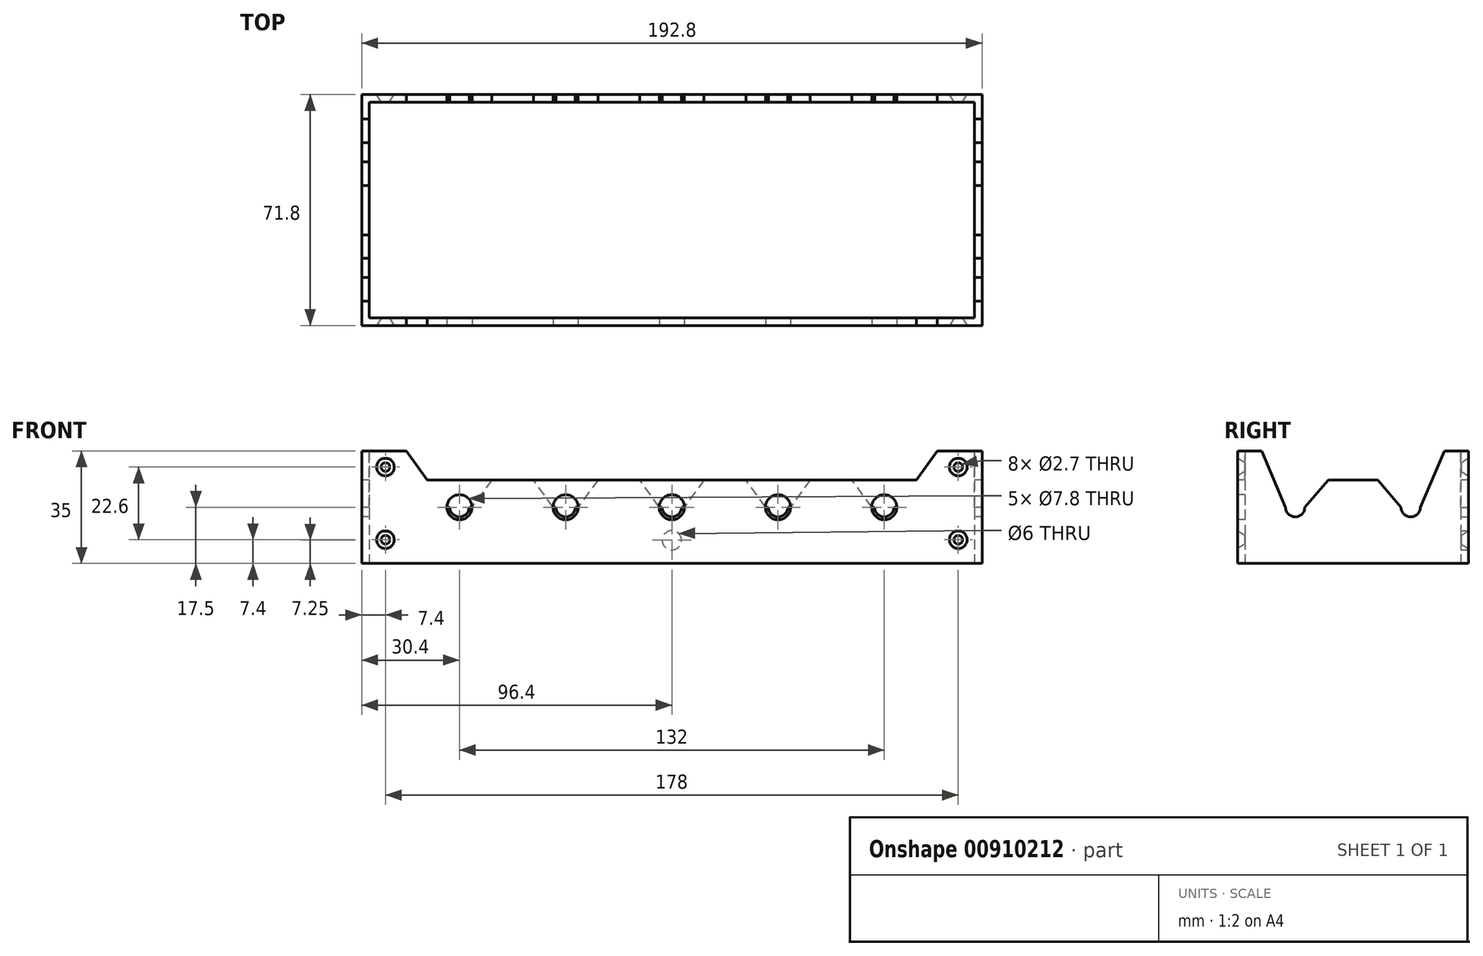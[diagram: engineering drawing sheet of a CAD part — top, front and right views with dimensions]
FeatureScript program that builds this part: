
annotation { "Feature Type Name" : "Feature", "Feature Type Description" : "" }
export const myFeature = defineFeature(function(context is Context, id is Id, definition is map)
    precondition{}
    {
        {
            var Q0;
            Q0=qCreatedBy(makeId("Top.planeOp"),FACE);
            var sketch = newSketch(context, id + "F0", { "sketchPlane" : qUnion([Q0])});
            skLineSegment(sketch, "E0.bottom", {"start": v(-94, 33.5) * mm, "end": v(94, 33.5) * mm});
            skLineSegment(sketch, "E0.top", {"start": v(-94, -33.5) * mm, "end": v(94, -33.5) * mm});
            skLineSegment(sketch, "E0.left", {"start": v(-94, 33.5) * mm, "end": v(-94, -33.5) * mm});
            skLineSegment(sketch, "E0.right", {"start": v(94, 33.5) * mm, "end": v(94, -33.5) * mm});
            skPoint(sketch, "E0.middle", {"position": v(0, 0) * mm});
            skLineSegment(sketch, "E1.bottom", {"start": v(-96.4, 35.9) * mm, "end": v(96.4, 35.9) * mm});
            skLineSegment(sketch, "E1.top", {"start": v(-96.4, -35.9) * mm, "end": v(96.4, -35.9) * mm});
            skLineSegment(sketch, "E1.left", {"start": v(-96.4, 35.9) * mm, "end": v(-96.4, -35.9) * mm});
            skLineSegment(sketch, "E1.right", {"start": v(96.4, 35.9) * mm, "end": v(96.4, -35.9) * mm});
            skSolve(sketch);
        }
        {
            var Q0;
            Q0=makeQuery(id+"F0.imprint","IMPRINT",FACE,{"disambiguationData":[TD([[makeQuery(id+"F0.imprint","IMPRINT",EDGE,{"derivedFrom":sQuery(id+"F0.wireOp",EDGE,"E0.bottom")}),1.0]])]});
            extrude(context, id + "F1", {"entities" : qUnion([Q0]), "depth" : 35 * mm, "offsetDistance" : 25 * mm});
        }
        {
            var Q0;
            Q0=makeQuery(id+"F1.opExtrude","SWEPT_FACE",FACE,{"disambiguationData":[OSD([sQuery(id+"F0.wireOp",EDGE,"E1.left")])]});
            var sketch = newSketch(context, id + "F2", { "sketchPlane" : qUnion([Q0])});
            skLineSegment(sketch, "E2", {"start": v(-35.9, 17.5) * mm, "end": v(35.9, 17.5) * mm, "construction": true});
            skPoint(sketch, "E3", {"position": v(0, 17.5) * mm});
            skLineSegment(sketch, "E4", {"start": v(-35.9, 17.5) * mm, "end": v(0, 17.5) * mm, "construction": true});
            skLineSegment(sketch, "E5", {"start": v(0, 17.5) * mm, "end": v(35.9, 17.5) * mm, "construction": true});
            skPoint(sketch, "E6", {"position": v(-17.95, 17.5) * mm});
            skPoint(sketch, "E7", {"position": v(17.95, 17.5) * mm});
            skCircle(sketch, "E8", {"center": v(-17.95, 17.5) * mm, "radius": 3 * mm});
            skCircle(sketch, "E9", {"center": v(17.95, 17.5) * mm, "radius": 3 * mm});
            skSolve(sketch);
        }
        {
            var Q0;
            Q0=makeQuery(id+"F2.imprint","IMPRINT",FACE,{"disambiguationData":[TD([[makeQuery(id+"F2.imprint","IMPRINT",EDGE,{"derivedFrom":sQuery(id+"F2.wireOp",EDGE,"E8")}),1.0]])]});
            var Q1;
            Q1=makeQuery(id+"F2.imprint","IMPRINT",FACE,{"disambiguationData":[TD([[makeQuery(id+"F2.imprint","IMPRINT",EDGE,{"derivedFrom":sQuery(id+"F2.wireOp",EDGE,"E9")}),1.0]])]});
            extrude(context, id + "F3", {"entities" : qUnion([Q0, Q1]), "operationType" : NewBodyOperationType.REMOVE, "endBound" : BoundingType.THROUGH_ALL, "oppositeDirection" : true, "depth" : 25 * mm, "offsetDistance" : 25 * mm});
        }
        {
            var Q0;
            Q0=makeQuery(id+"F1.opExtrude","SWEPT_FACE",FACE,{"disambiguationData":[OSD([sQuery(id+"F0.wireOp",EDGE,"E1.top")])]});
            var sketch = newSketch(context, id + "F4", { "sketchPlane" : qUnion([Q0])});
            skLineSegment(sketch, "E10", {"start": v(0, 35) * mm, "end": v(0, 0) * mm, "construction": true});
            skPoint(sketch, "E11", {"position": v(0, 17.5) * mm});
            skCircle(sketch, "E12", {"center": v(0, 17.5) * mm, "radius": 3.9 * mm});
            skCircle(sketch, "E13.1.0.0", {"center": v(33, 17.5) * mm, "radius": 3.9 * mm});
            skCircle(sketch, "E13.2.0.0", {"center": v(66, 17.5) * mm, "radius": 3.9 * mm});
            skLineSegment(sketch, "E13.direction1", {"start": v(0, 17.5) * mm, "end": v(33, 17.5) * mm, "construction": true});
            skCircle(sketch, "E14.1.0.0", {"center": v(-33, 17.5) * mm, "radius": 3.9 * mm});
            skCircle(sketch, "E14.2.0.0", {"center": v(-66, 17.5) * mm, "radius": 3.9 * mm});
            skLineSegment(sketch, "E14.direction1", {"start": v(0, 17.5) * mm, "end": v(-33, 17.5) * mm, "construction": true});
            skSolve(sketch);
        }
        {
            var Q0;
            Q0=qSketchRegion(id+"F4",true);
            extrude(context, id + "F5", {"entities" : qUnion([Q0]), "operationType" : NewBodyOperationType.REMOVE, "oppositeDirection" : true, "depth" : 25 * mm, "offsetDistance" : 25 * mm});
        }
        {
            var Q0;
            Q0=makeQuery(id+"F1.opExtrude","SWEPT_FACE",FACE,{"disambiguationData":[OSD([sQuery(id+"F0.wireOp",EDGE,"E1.bottom")])]});
            var sketch = newSketch(context, id + "F6", { "sketchPlane" : qUnion([Q0])});
            skLineSegment(sketch, "E15", {"start": v(0, 35) * mm, "end": v(0, 0) * mm, "construction": true});
            skLineSegment(sketch, "E16", {"start": v(-96.4, 17.5) * mm, "end": v(96.4, 17.5) * mm, "construction": true});
            skPoint(sketch, "E17", {"position": v(0, 17.5) * mm});
            skCircle(sketch, "E18", {"center": v(0, 17.5) * mm, "radius": 3 * mm});
            skCircle(sketch, "E19.1.0.0", {"center": v(33, 17.5) * mm, "radius": 3 * mm});
            skCircle(sketch, "E19.2.0.0", {"center": v(66, 17.5) * mm, "radius": 3 * mm});
            skLineSegment(sketch, "E19.direction1", {"start": v(0, 17.5) * mm, "end": v(33, 17.5) * mm, "construction": true});
            skCircle(sketch, "E20.1.0.0", {"center": v(-33, 17.5) * mm, "radius": 3 * mm});
            skCircle(sketch, "E20.2.0.0", {"center": v(-66, 17.5) * mm, "radius": 3 * mm});
            skLineSegment(sketch, "E20.direction1", {"start": v(0, 17.5) * mm, "end": v(-33, 17.5) * mm, "construction": true});
            skSolve(sketch);
        }
        {
            var Q0;
            Q0=qSketchRegion(id+"F6",true);
            extrude(context, id + "F7", {"entities" : qUnion([Q0]), "operationType" : NewBodyOperationType.REMOVE, "oppositeDirection" : true, "depth" : 25 * mm, "offsetDistance" : 25 * mm});
        }
        {
            var Q0;
            Q0=makeQuery(id+"F1.opExtrude","CAP_FACE",FACE,{"disambiguationData":[OSD([sQuery(id+"F0.wireOp",EDGE,"E0.bottom"),sQuery(id+"F0.wireOp",EDGE,"E0.top"),sQuery(id+"F0.wireOp",EDGE,"E0.left"),sQuery(id+"F0.wireOp",EDGE,"E0.right"),sQuery(id+"F0.wireOp",EDGE,"E1.bottom"),sQuery(id+"F0.wireOp",EDGE,"E1.top"),sQuery(id+"F0.wireOp",EDGE,"E1.left"),sQuery(id+"F0.wireOp",EDGE,"E1.right")])],"isStart":false});
            var sketch = newSketch(context, id + "F8", { "sketchPlane" : qUnion([Q0])});
            skLineSegment(sketch, "E21", {"start": v(96.4, 0) * mm, "end": v(-96.4, 0) * mm, "construction": true});
            skLineSegment(sketch, "E22", {"start": v(0, -33.5) * mm, "end": v(0, 33.5) * mm, "construction": true});
            skLineSegment(sketch, "E23", {"start": v(96.4, -35.9) * mm, "end": v(96.4, 0) * mm, "construction": true});
            skLineSegment(sketch, "E24", {"start": v(96.4, 35.9) * mm, "end": v(96.4, 0) * mm, "construction": true});
            skLineSegment(sketch, "E25", {"start": v(-96.4, -35.9) * mm, "end": v(-96.4, 0) * mm, "construction": true});
            skLineSegment(sketch, "E26", {"start": v(-96.4, 35.9) * mm, "end": v(-96.4, 0) * mm, "construction": true});
            skPoint(sketch, "E27", {"position": v(96.4, -17.95) * mm});
            skPoint(sketch, "E28", {"position": v(96.4, 17.95) * mm});
            skPoint(sketch, "E29", {"position": v(-96.4, -17.95) * mm});
            skPoint(sketch, "E30", {"position": v(-96.4, 17.95) * mm});
            skCircle(sketch, "E31", {"center": v(-96.4, 35.9) * mm, "radius": 7.5 * mm, "construction": true});
            skCircle(sketch, "E32", {"center": v(-96.4, -35.9) * mm, "radius": 7.5 * mm, "construction": true});
            skCircle(sketch, "E33", {"center": v(96.4, 35.9) * mm, "radius": 7.5 * mm, "construction": true});
            skCircle(sketch, "E34", {"center": v(96.4, -35.9) * mm, "radius": 7.5 * mm, "construction": true});
            skPoint(sketch, "E35", {"position": v(-96.4, 28.4) * mm});
            skPoint(sketch, "E36", {"position": v(-96.4, -28.4) * mm});
            skPoint(sketch, "E37", {"position": v(96.4, 28.4) * mm});
            skPoint(sketch, "E38", {"position": v(96.4, -28.4) * mm});
            skPoint(sketch, "E39", {"position": v(0, 35.9) * mm});
            skPoint(sketch, "E40", {"position": v(0, -35.9) * mm});
            skPoint(sketch, "E41.1.0.0", {"position": v(33, 35.9) * mm});
            skPoint(sketch, "E41.2.0.0", {"position": v(66, 35.9) * mm});
            skLineSegment(sketch, "E41.direction1", {"start": v(0, 35.9) * mm, "end": v(33, 35.9) * mm, "construction": true});
            skPoint(sketch, "E42.1.0.0", {"position": v(-33, 35.9) * mm});
            skPoint(sketch, "E42.2.0.0", {"position": v(-66, 35.9) * mm});
            skLineSegment(sketch, "E42.direction1", {"start": v(0, 35.9) * mm, "end": v(-33, 35.9) * mm, "construction": true});
            skPoint(sketch, "E43.1.0.0", {"position": v(33, -35.9) * mm});
            skPoint(sketch, "E43.2.0.0", {"position": v(66, -35.9) * mm});
            skLineSegment(sketch, "E43.direction1", {"start": v(0, -35.9) * mm, "end": v(33, -35.9) * mm, "construction": true});
            skPoint(sketch, "E44.1.0.0", {"position": v(-33, -35.9) * mm});
            skPoint(sketch, "E44.2.0.0", {"position": v(-66, -35.9) * mm});
            skLineSegment(sketch, "E44.direction1", {"start": v(0, -35.9) * mm, "end": v(-33, -35.9) * mm, "construction": true});
            skSolve(sketch);
        }
        {
            var Q0;
            Q0=makeQuery(id+"F1.opExtrude","SWEPT_FACE",FACE,{"disambiguationData":[OSD([sQuery(id+"F0.wireOp",EDGE,"E1.left")])]});
            var sketch = newSketch(context, id + "F9", { "sketchPlane" : qUnion([Q0])});
            skPoint(sketch, "E45", {"position": v(-20.95, 17.5) * mm});
            skPoint(sketch, "E45.positionSnap0", {"position": v(-35.9, 17.5) * mm});
            skPoint(sketch, "E46", {"position": v(20.95, 17.5) * mm});
            skPoint(sketch, "E46.positionSnap0", {"position": v(35.9, 17.5) * mm});
            skPoint(sketch, "E47", {"position": v(14.95, 17.5) * mm});
            skPoint(sketch, "E48", {"position": v(-14.95, 17.5) * mm});
            skLineSegment(sketch, "E49", {"start": v(-28.37, 35) * mm, "end": v(-20.95, 17.5) * mm});
            skLineSegment(sketch, "E50", {"start": v(-14.95, 17.5) * mm, "end": v(0, 35) * mm});
            skLineSegment(sketch, "E51", {"start": v(0, 35) * mm, "end": v(14.95, 17.5) * mm});
            skLineSegment(sketch, "E52", {"start": v(20.95, 17.5) * mm, "end": v(28.32, 35) * mm});
            skLineSegment(sketch, "E53", {"start": v(-35.9, 26) * mm, "end": v(35.9, 26) * mm});
            skSolve(sketch);
        }
        {
            var Q0;
            Q0=makeQuery(id+"F1.opExtrude","SWEPT_FACE",FACE,{"disambiguationData":[OSD([sQuery(id+"F0.wireOp",EDGE,"E1.top")])]});
            var sketch = newSketch(context, id + "F10", { "sketchPlane" : qUnion([Q0])});
            skPoint(sketch, "E54", {"position": v(-69.9, 17.5) * mm});
            skPoint(sketch, "E54.positionSnap0", {"position": v(-96.4, 17.5) * mm});
            skPoint(sketch, "E55", {"position": v(-62.1, 17.5) * mm});
            skPoint(sketch, "E56", {"position": v(-36.9, 17.5) * mm});
            skPoint(sketch, "E57", {"position": v(-29.1, 17.5) * mm});
            skPoint(sketch, "E58", {"position": v(-3.9, 17.5) * mm});
            skPoint(sketch, "E59", {"position": v(3.9, 17.5) * mm});
            skPoint(sketch, "E60", {"position": v(29.1, 17.5) * mm});
            skPoint(sketch, "E61", {"position": v(36.9, 17.5) * mm});
            skPoint(sketch, "E62", {"position": v(62.1, 17.5) * mm});
            skPoint(sketch, "E63", {"position": v(69.9, 17.5) * mm});
            skPoint(sketch, "E64", {"position": v(0, 35) * mm});
            skPoint(sketch, "E65.1.0.0", {"position": v(16.5, 35) * mm});
            skPoint(sketch, "E65.2.0.0", {"position": v(33, 35) * mm});
            skPoint(sketch, "E65.3.0.0", {"position": v(49.5, 35) * mm});
            skPoint(sketch, "E65.4.0.0", {"position": v(66, 35) * mm});
            skPoint(sketch, "E65.5.0.0", {"position": v(82.5, 35) * mm});
            skLineSegment(sketch, "E65.direction1", {"start": v(0, 35) * mm, "end": v(16.5, 35) * mm, "construction": true});
            skPoint(sketch, "E66.1.0.0", {"position": v(-16.5, 35) * mm});
            skPoint(sketch, "E66.2.0.0", {"position": v(-33, 35) * mm});
            skPoint(sketch, "E66.3.0.0", {"position": v(-49.5, 35) * mm});
            skPoint(sketch, "E66.4.0.0", {"position": v(-66, 35) * mm});
            skPoint(sketch, "E66.5.0.0", {"position": v(-82.5, 35) * mm});
            skLineSegment(sketch, "E66.direction1", {"start": v(0, 35) * mm, "end": v(-16.5, 35) * mm, "construction": true});
            skLineSegment(sketch, "E67", {"start": v(-82.5, 35) * mm, "end": v(-69.9, 17.5) * mm});
            skLineSegment(sketch, "E68", {"start": v(-69.9, 17.5) * mm, "end": v(-62.1, 17.5) * mm});
            skLineSegment(sketch, "E69", {"start": v(-62.1, 17.5) * mm, "end": v(-49.5, 35) * mm});
            skLineSegment(sketch, "E70", {"start": v(-49.5, 35) * mm, "end": v(-36.9, 17.5) * mm});
            skLineSegment(sketch, "E71", {"start": v(-36.9, 17.5) * mm, "end": v(-29.1, 17.5) * mm});
            skLineSegment(sketch, "E72", {"start": v(-29.1, 17.5) * mm, "end": v(-16.5, 35) * mm});
            skLineSegment(sketch, "E73", {"start": v(-16.5, 35) * mm, "end": v(-3.9, 17.5) * mm});
            skLineSegment(sketch, "E74", {"start": v(-3.9, 17.5) * mm, "end": v(3.9, 17.5) * mm});
            skLineSegment(sketch, "E75", {"start": v(3.9, 17.5) * mm, "end": v(16.5, 35) * mm});
            skLineSegment(sketch, "E76", {"start": v(16.5, 35) * mm, "end": v(29.1, 17.5) * mm});
            skLineSegment(sketch, "E77", {"start": v(29.1, 17.5) * mm, "end": v(36.9, 17.5) * mm});
            skLineSegment(sketch, "E78", {"start": v(36.9, 17.5) * mm, "end": v(49.5, 35) * mm});
            skLineSegment(sketch, "E79", {"start": v(49.5, 35) * mm, "end": v(62.1, 17.5) * mm});
            skLineSegment(sketch, "E80", {"start": v(62.1, 17.5) * mm, "end": v(69.9, 17.5) * mm});
            skLineSegment(sketch, "E81", {"start": v(69.9, 17.5) * mm, "end": v(82.5, 35) * mm});
            skLineSegment(sketch, "E82", {"start": v(-96.4, 26) * mm, "end": v(96.4, 26) * mm});
            skLineSegment(sketch, "E83.bottom", {"start": v(-94, 2.4) * mm, "end": v(-84, 2.4) * mm});
            skLineSegment(sketch, "E83.top", {"start": v(-94, 12.4) * mm, "end": v(-84, 12.4) * mm});
            skLineSegment(sketch, "E83.left", {"start": v(-94, 2.4) * mm, "end": v(-94, 12.4) * mm});
            skLineSegment(sketch, "E83.right", {"start": v(-84, 2.4) * mm, "end": v(-84, 12.4) * mm});
            skLineSegment(sketch, "E84.bottom", {"start": v(84, 12.4) * mm, "end": v(94, 12.4) * mm});
            skLineSegment(sketch, "E84.top", {"start": v(84, 2.4) * mm, "end": v(94, 2.4) * mm});
            skLineSegment(sketch, "E84.left", {"start": v(84, 12.4) * mm, "end": v(84, 2.4) * mm});
            skLineSegment(sketch, "E84.right", {"start": v(94, 12.4) * mm, "end": v(94, 2.4) * mm});
            skLineSegment(sketch, "E85.bottom", {"start": v(-94, 35) * mm, "end": v(-84, 35) * mm});
            skLineSegment(sketch, "E85.top", {"start": v(-94, 25) * mm, "end": v(-84, 25) * mm});
            skLineSegment(sketch, "E85.left", {"start": v(-94, 35) * mm, "end": v(-94, 25) * mm});
            skLineSegment(sketch, "E85.right", {"start": v(-84, 35) * mm, "end": v(-84, 25) * mm});
            skLineSegment(sketch, "E86.bottom", {"start": v(84, 25) * mm, "end": v(94, 25) * mm});
            skLineSegment(sketch, "E86.top", {"start": v(84, 35) * mm, "end": v(94, 35) * mm});
            skLineSegment(sketch, "E86.left", {"start": v(84, 25) * mm, "end": v(84, 35) * mm});
            skLineSegment(sketch, "E86.right", {"start": v(94, 25) * mm, "end": v(94, 35) * mm});
            skPoint(sketch, "E87", {"position": v(-89, 30) * mm});
            skPoint(sketch, "E87.positionSnap0", {"position": v(-84, 30) * mm});
            skPoint(sketch, "E87.positionSnap1", {"position": v(-89, 25) * mm});
            skPoint(sketch, "E88", {"position": v(-89, 7.4) * mm});
            skPoint(sketch, "E88.positionSnap0", {"position": v(-84, 7.4) * mm});
            skPoint(sketch, "E89", {"position": v(89, 30) * mm});
            skPoint(sketch, "E89.positionSnap0", {"position": v(89, 35) * mm});
            skPoint(sketch, "E89.positionSnap1", {"position": v(94, 30) * mm});
            skPoint(sketch, "E90", {"position": v(89, 7.4) * mm});
            skPoint(sketch, "E90.positionSnap0", {"position": v(94, 7.4) * mm});
            skPoint(sketch, "E90.positionSnap1", {"position": v(89, 12.4) * mm});
            skSolve(sketch);
        }
        {
            var Q0;
            {var subQ0=sQuery(id+"F9.wireOp",EDGE,"E49");var subQ1=makeQuery(id+"F3.boolean.opBoolean","COPY",EDGE,{"derivedFrom":makeQuery(id+"F3.opExtrude","CAP_EDGE",EDGE,{"disambiguationData":[OSD([sQuery(id+"F2.wireOp",EDGE,"E8")])],"isStart":true})});var subQ2=makeQuery(id+"F9.imprint","INTERSECT",VERTEX,{"derivedFrom":[subQ1,subQ0]});Q0=makeQuery(id+"F9.imprint","IMPRINT",FACE,{"disambiguationData":[TD([[makeQuery(id+"F9.imprint","IMPRINT",EDGE,{"disambiguationData":[TD([[subQ2,1.0]])],"derivedFrom":subQ0}),1.0]])]});}
            var Q1;
            {var subQ0=sQuery(id+"F9.wireOp",EDGE,"E49");var subQ1=makeQuery(id+"F1.opExtrude","CAP_EDGE",EDGE,{"disambiguationData":[OSD([sQuery(id+"F0.wireOp",EDGE,"E1.left")])],"isStart":false});var subQ2=makeQuery(id+"F9.imprint","INTERSECT",VERTEX,{"derivedFrom":[subQ1,subQ0]});Q1=makeQuery(id+"F9.imprint","IMPRINT",FACE,{"disambiguationData":[TD([[makeQuery(id+"F9.imprint","IMPRINT",EDGE,{"disambiguationData":[TD([[subQ2,-1.0]])],"derivedFrom":subQ0}),1.0]])]});}
            var Q2;
            {var subQ1=makeQuery(id+"F1.opExtrude","CAP_EDGE",EDGE,{"disambiguationData":[OSD([sQuery(id+"F0.wireOp",EDGE,"E1.left")])],"isStart":false});var subQ5=sQuery(id+"F9.wireOp",EDGE,"E52");var subQ6=makeQuery(id+"F9.imprint","INTERSECT",VERTEX,{"derivedFrom":[subQ1,subQ5]});Q2=makeQuery(id+"F9.imprint","IMPRINT",FACE,{"disambiguationData":[TD([[makeQuery(id+"F9.imprint","IMPRINT",EDGE,{"disambiguationData":[TD([[subQ6,1.0]])],"derivedFrom":subQ5}),1.0]])]});}
            var Q3;
            {var subQ0=sQuery(id+"F9.wireOp",EDGE,"E51");var subQ1=makeQuery(id+"F3.boolean.opBoolean","COPY",EDGE,{"derivedFrom":makeQuery(id+"F3.opExtrude","CAP_EDGE",EDGE,{"disambiguationData":[OSD([sQuery(id+"F2.wireOp",EDGE,"E9")])],"isStart":true})});var subQ2=makeQuery(id+"F9.imprint","INTERSECT",VERTEX,{"derivedFrom":[subQ1,subQ0]});Q3=makeQuery(id+"F9.imprint","IMPRINT",FACE,{"disambiguationData":[TD([[makeQuery(id+"F9.imprint","IMPRINT",EDGE,{"disambiguationData":[TD([[subQ2,1.0]])],"derivedFrom":subQ0}),1.0]])]});}
            var Q4;
            {var subQ1=sQuery(id+"F9.wireOp",EDGE,"E50");var subQ3=sQuery(id+"F9.wireOp",EDGE,"E53");var subQ4=makeQuery(id+"F9.imprint","INTERSECT",VERTEX,{"derivedFrom":[subQ1,subQ3]});Q4=makeQuery(id+"F9.imprint","IMPRINT",FACE,{"disambiguationData":[TD([[makeQuery(id+"F9.imprint","IMPRINT",EDGE,{"disambiguationData":[TD([[subQ4,-1.0]])],"derivedFrom":subQ3}),1.0]])]});}
            extrude(context, id + "F11", {"entities" : qUnion([Q0, Q1, Q2, Q3, Q4]), "operationType" : NewBodyOperationType.REMOVE, "endBound" : BoundingType.THROUGH_ALL, "oppositeDirection" : true, "depth" : 25 * mm, "offsetDistance" : 25 * mm});
        }
        {
            var Q0;
            {var subQ0=sQuery(id+"F10.wireOp",EDGE,"E67");var subQ1=makeQuery(id+"F1.opExtrude","CAP_EDGE",EDGE,{"disambiguationData":[OSD([sQuery(id+"F0.wireOp",EDGE,"E1.top")])],"isStart":false});var subQ2=makeQuery(id+"F10.imprint","INTERSECT",VERTEX,{"derivedFrom":[subQ1,subQ0]});Q0=makeQuery(id+"F10.imprint","IMPRINT",FACE,{"disambiguationData":[TD([[makeQuery(id+"F10.imprint","IMPRINT",EDGE,{"disambiguationData":[TD([[subQ2,-1.0]])],"derivedFrom":subQ0}),1.0]])]});}
            var Q1;
            {var subQ0=sQuery(id+"F10.wireOp",EDGE,"E70");var subQ3=sQuery(id+"F10.wireOp",EDGE,"E82");var subQ4=makeQuery(id+"F10.imprint","INTERSECT",VERTEX,{"derivedFrom":[subQ0,subQ3]});Q1=makeQuery(id+"F10.imprint","IMPRINT",FACE,{"disambiguationData":[TD([[makeQuery(id+"F10.imprint","IMPRINT",EDGE,{"disambiguationData":[TD([[subQ4,-1.0]])],"derivedFrom":subQ3}),1.0]])]});}
            var Q2;
            {var subQ1=sQuery(id+"F10.wireOp",EDGE,"E69");var subQ3=sQuery(id+"F10.wireOp",EDGE,"E82");var subQ4=makeQuery(id+"F10.imprint","INTERSECT",VERTEX,{"derivedFrom":[subQ1,subQ3]});Q2=makeQuery(id+"F10.imprint","IMPRINT",FACE,{"disambiguationData":[TD([[makeQuery(id+"F10.imprint","IMPRINT",EDGE,{"disambiguationData":[TD([[subQ4,-1.0]])],"derivedFrom":subQ3}),1.0]])]});}
            var Q3;
            {var subQ0=sQuery(id+"F10.wireOp",EDGE,"E73");var subQ3=sQuery(id+"F10.wireOp",EDGE,"E82");var subQ4=makeQuery(id+"F10.imprint","INTERSECT",VERTEX,{"derivedFrom":[subQ0,subQ3]});Q3=makeQuery(id+"F10.imprint","IMPRINT",FACE,{"disambiguationData":[TD([[makeQuery(id+"F10.imprint","IMPRINT",EDGE,{"disambiguationData":[TD([[subQ4,-1.0]])],"derivedFrom":subQ3}),1.0]])]});}
            var Q4;
            {var subQ1=sQuery(id+"F10.wireOp",EDGE,"E72");var subQ3=sQuery(id+"F10.wireOp",EDGE,"E82");var subQ4=makeQuery(id+"F10.imprint","INTERSECT",VERTEX,{"derivedFrom":[subQ1,subQ3]});Q4=makeQuery(id+"F10.imprint","IMPRINT",FACE,{"disambiguationData":[TD([[makeQuery(id+"F10.imprint","IMPRINT",EDGE,{"disambiguationData":[TD([[subQ4,-1.0]])],"derivedFrom":subQ3}),1.0]])]});}
            var Q5;
            {var subQ0=sQuery(id+"F10.wireOp",EDGE,"E76");var subQ3=sQuery(id+"F10.wireOp",EDGE,"E82");var subQ4=makeQuery(id+"F10.imprint","INTERSECT",VERTEX,{"derivedFrom":[subQ0,subQ3]});Q5=makeQuery(id+"F10.imprint","IMPRINT",FACE,{"disambiguationData":[TD([[makeQuery(id+"F10.imprint","IMPRINT",EDGE,{"disambiguationData":[TD([[subQ4,-1.0]])],"derivedFrom":subQ3}),1.0]])]});}
            var Q6;
            {var subQ1=sQuery(id+"F10.wireOp",EDGE,"E78");var subQ3=sQuery(id+"F10.wireOp",EDGE,"E82");var subQ4=makeQuery(id+"F10.imprint","INTERSECT",VERTEX,{"derivedFrom":[subQ1,subQ3]});Q6=makeQuery(id+"F10.imprint","IMPRINT",FACE,{"disambiguationData":[TD([[makeQuery(id+"F10.imprint","IMPRINT",EDGE,{"disambiguationData":[TD([[subQ4,-1.0]])],"derivedFrom":subQ3}),1.0]])]});}
            var Q7;
            {var subQ1=makeQuery(id+"F1.opExtrude","CAP_EDGE",EDGE,{"disambiguationData":[OSD([sQuery(id+"F0.wireOp",EDGE,"E1.top")])],"isStart":false});var subQ5=sQuery(id+"F10.wireOp",EDGE,"E81");var subQ6=makeQuery(id+"F10.imprint","INTERSECT",VERTEX,{"derivedFrom":[subQ1,subQ5]});Q7=makeQuery(id+"F10.imprint","IMPRINT",FACE,{"disambiguationData":[TD([[makeQuery(id+"F10.imprint","IMPRINT",EDGE,{"disambiguationData":[TD([[subQ6,1.0]])],"derivedFrom":subQ5}),1.0]])]});}
            var Q8;
            {var subQ0=sQuery(id+"F10.wireOp",EDGE,"E80");Q8=makeQuery(id+"F10.imprint","IMPRINT",FACE,{"disambiguationData":[TD([[makeQuery(id+"F10.imprint","IMPRINT",EDGE,{"derivedFrom":subQ0}),1.0]])]});}
            var Q9;
            {var subQ0=sQuery(id+"F10.wireOp",EDGE,"E77");Q9=makeQuery(id+"F10.imprint","IMPRINT",FACE,{"disambiguationData":[TD([[makeQuery(id+"F10.imprint","IMPRINT",EDGE,{"derivedFrom":subQ0}),1.0]])]});}
            var Q10;
            {var subQ0=sQuery(id+"F10.wireOp",EDGE,"E74");Q10=makeQuery(id+"F10.imprint","IMPRINT",FACE,{"disambiguationData":[TD([[makeQuery(id+"F10.imprint","IMPRINT",EDGE,{"derivedFrom":subQ0}),1.0]])]});}
            var Q11;
            {var subQ0=sQuery(id+"F10.wireOp",EDGE,"E71");Q11=makeQuery(id+"F10.imprint","IMPRINT",FACE,{"disambiguationData":[TD([[makeQuery(id+"F10.imprint","IMPRINT",EDGE,{"derivedFrom":subQ0}),1.0]])]});}
            var Q12;
            {var subQ0=sQuery(id+"F10.wireOp",EDGE,"E68");Q12=makeQuery(id+"F10.imprint","IMPRINT",FACE,{"disambiguationData":[TD([[makeQuery(id+"F10.imprint","IMPRINT",EDGE,{"derivedFrom":subQ0}),1.0]])]});}
            var Q13;
            {var subQ1=sQuery(id+"F10.wireOp",EDGE,"E75");var subQ3=sQuery(id+"F10.wireOp",EDGE,"E82");var subQ4=makeQuery(id+"F10.imprint","INTERSECT",VERTEX,{"derivedFrom":[subQ1,subQ3]});Q13=makeQuery(id+"F10.imprint","IMPRINT",FACE,{"disambiguationData":[TD([[makeQuery(id+"F10.imprint","IMPRINT",EDGE,{"disambiguationData":[TD([[subQ4,-1.0]])],"derivedFrom":subQ3}),1.0]])]});}
            extrude(context, id + "F12", {"entities" : qUnion([Q0, Q1, Q2, Q3, Q4, Q5, Q6, Q7, Q8, Q9, Q10, Q11, Q12, Q13]), "operationType" : NewBodyOperationType.REMOVE, "endBound" : BoundingType.THROUGH_ALL, "oppositeDirection" : true, "depth" : 25 * mm, "offsetDistance" : 25 * mm});
        }
        {
            var Q0;
            Q0=sQuery(id+"F10.wireOp",VERTEX,"E87");
            var Q1;
            Q1=sQuery(id+"F10.wireOp",VERTEX,"E88");
            var Q2;
            Q2=sQuery(id+"F10.wireOp",VERTEX,"E89");
            var Q3;
            Q3=sQuery(id+"F10.wireOp",VERTEX,"E90");
            var Q4;
            Q4=makeQuery(id+"F1.opExtrude","SWEPT_BODY",BODY,{"disambiguationData":[OSD([sQuery(id+"F0.wireOp",EDGE,"E0.bottom"),sQuery(id+"F0.wireOp",EDGE,"E0.top"),sQuery(id+"F0.wireOp",EDGE,"E0.left"),sQuery(id+"F0.wireOp",EDGE,"E0.right"),sQuery(id+"F0.wireOp",EDGE,"E1.bottom"),sQuery(id+"F0.wireOp",EDGE,"E1.top"),sQuery(id+"F0.wireOp",EDGE,"E1.left"),sQuery(id+"F0.wireOp",EDGE,"E1.right")])]});
            hole(context, id + "F13", {"style" : HoleStyle.C_SINK, "endStyle" : HoleEndStyle.BLIND, "holeDiameter" : 2.7 * mm, "cSinkDiameter" : 5.5 * mm, "cSinkAngle" : 63 * degree, "majorDiameter" : 5 * mm, "holeDepth" : 12 * mm, "isTappedThrough" : true, "tappedDepth" : 12 * mm, "tapClearance" : 3, "locations" : qUnion([Q0, Q1, Q2, Q3]), "scope" : qUnion([Q4])});
        }
        {
            var Q0;
            Q0=makeQuery(id+"F1.opExtrude","SWEPT_FACE",FACE,{"disambiguationData":[OSD([sQuery(id+"F0.wireOp",EDGE,"E1.bottom")])]});
            var sketch = newSketch(context, id + "F14", { "sketchPlane" : qUnion([Q0])});
            skPoint(sketch, "E91", {"position": v(-89, 30) * mm});
            skPoint(sketch, "E92", {"position": v(-89, 7.4) * mm});
            skPoint(sketch, "E93", {"position": v(89, 7.4) * mm});
            skPoint(sketch, "E94", {"position": v(89, 30) * mm});
            skSolve(sketch);
        }
        {
            var Q0;
            Q0=sQuery(id+"F14.wireOp",VERTEX,"E94");
            var Q1;
            Q1=sQuery(id+"F14.wireOp",VERTEX,"E93");
            var Q2;
            Q2=sQuery(id+"F14.wireOp",VERTEX,"E91");
            var Q3;
            Q3=sQuery(id+"F14.wireOp",VERTEX,"E92");
            var Q4;
            Q4=makeQuery(id+"F1.opExtrude","SWEPT_BODY",BODY,{"disambiguationData":[OSD([sQuery(id+"F0.wireOp",EDGE,"E0.bottom"),sQuery(id+"F0.wireOp",EDGE,"E0.top"),sQuery(id+"F0.wireOp",EDGE,"E0.left"),sQuery(id+"F0.wireOp",EDGE,"E0.right"),sQuery(id+"F0.wireOp",EDGE,"E1.bottom"),sQuery(id+"F0.wireOp",EDGE,"E1.top"),sQuery(id+"F0.wireOp",EDGE,"E1.left"),sQuery(id+"F0.wireOp",EDGE,"E1.right")])]});
            hole(context, id + "F15", {"style" : HoleStyle.C_SINK, "endStyle" : HoleEndStyle.BLIND, "holeDiameter" : 2.7 * mm, "cSinkDiameter" : 5.5 * mm, "cSinkAngle" : 63 * degree, "majorDiameter" : 5 * mm, "holeDepth" : 12 * mm, "isTappedThrough" : true, "tappedDepth" : 12 * mm, "tapClearance" : 3, "locations" : qUnion([Q0, Q1, Q2, Q3]), "scope" : qUnion([Q4])});
        }
        {
            var Q0;
            {var subQ1=sQuery(id+"F10.wireOp",EDGE,"E67");var subQ4=sQuery(id+"F10.wireOp",EDGE,"E82");var subQ5=makeQuery(id+"F10.imprint","INTERSECT",VERTEX,{"derivedFrom":[subQ1,subQ4]});Q0=makeQuery(id+"F10.imprint","IMPRINT",FACE,{"disambiguationData":[TD([[makeQuery(id+"F10.imprint","IMPRINT",EDGE,{"disambiguationData":[TD([[subQ5,-1.0]])],"derivedFrom":subQ4}),-1.0]])]});}
            var Q1;
            {var subQ1=sQuery(id+"F10.wireOp",EDGE,"E70");var subQ4=sQuery(id+"F10.wireOp",EDGE,"E82");var subQ5=makeQuery(id+"F10.imprint","INTERSECT",VERTEX,{"derivedFrom":[subQ1,subQ4]});Q1=makeQuery(id+"F10.imprint","IMPRINT",FACE,{"disambiguationData":[TD([[makeQuery(id+"F10.imprint","IMPRINT",EDGE,{"disambiguationData":[TD([[subQ5,-1.0]])],"derivedFrom":subQ4}),-1.0]])]});}
            var Q2;
            {var subQ1=sQuery(id+"F10.wireOp",EDGE,"E73");var subQ4=sQuery(id+"F10.wireOp",EDGE,"E82");var subQ5=makeQuery(id+"F10.imprint","INTERSECT",VERTEX,{"derivedFrom":[subQ1,subQ4]});Q2=makeQuery(id+"F10.imprint","IMPRINT",FACE,{"disambiguationData":[TD([[makeQuery(id+"F10.imprint","IMPRINT",EDGE,{"disambiguationData":[TD([[subQ5,-1.0]])],"derivedFrom":subQ4}),-1.0]])]});}
            var Q3;
            {var subQ1=sQuery(id+"F10.wireOp",EDGE,"E76");var subQ4=sQuery(id+"F10.wireOp",EDGE,"E82");var subQ5=makeQuery(id+"F10.imprint","INTERSECT",VERTEX,{"derivedFrom":[subQ1,subQ4]});Q3=makeQuery(id+"F10.imprint","IMPRINT",FACE,{"disambiguationData":[TD([[makeQuery(id+"F10.imprint","IMPRINT",EDGE,{"disambiguationData":[TD([[subQ5,-1.0]])],"derivedFrom":subQ4}),-1.0]])]});}
            var Q4;
            {var subQ1=sQuery(id+"F10.wireOp",EDGE,"E79");var subQ4=sQuery(id+"F10.wireOp",EDGE,"E82");var subQ5=makeQuery(id+"F10.imprint","INTERSECT",VERTEX,{"derivedFrom":[subQ1,subQ4]});Q4=makeQuery(id+"F10.imprint","IMPRINT",FACE,{"disambiguationData":[TD([[makeQuery(id+"F10.imprint","IMPRINT",EDGE,{"disambiguationData":[TD([[subQ5,-1.0]])],"derivedFrom":subQ4}),-1.0]])]});}
            extrude(context, id + "F16", {"entities" : qUnion([Q0, Q1, Q2, Q3, Q4]), "operationType" : NewBodyOperationType.REMOVE, "oppositeDirection" : true, "depth" : 130.4 * mm, "offsetDistance" : 25 * mm, "hasSecondDirection" : true, "secondDirectionOppositeDirection" : true, "secondDirectionDepth" : 18.1 * mm});
        }
        {
            var Q0;
            Q0=makeQuery(id+"F1.opExtrude","SWEPT_FACE",FACE,{"disambiguationData":[OSD([sQuery(id+"F0.wireOp",EDGE,"E1.bottom")])]});
            var sketch = newSketch(context, id + "F17", { "sketchPlane" : qUnion([Q0])});
            skLineSegment(sketch, "E95", {"start": v(0, 14.5) * mm, "end": v(0, 0) * mm, "construction": true});
            skPoint(sketch, "E96", {"position": v(0, 7.25) * mm});
            skCircle(sketch, "E97", {"center": v(0, 7.25) * mm, "radius": 3 * mm});
            skSolve(sketch);
        }
        {
            var Q0;
            Q0=makeQuery(id+"F17.imprint","IMPRINT",FACE,{"disambiguationData":[TD([[makeQuery(id+"F17.imprint","IMPRINT",EDGE,{"derivedFrom":sQuery(id+"F17.wireOp",EDGE,"E97")}),1.0]])]});
            var Q1;
            Q1=sQuery(id+"F17.wireOp",EDGE,"E97");
            extrude(context, id + "F18", {"entities" : qUnion([Q0]), "operationType" : NewBodyOperationType.REMOVE, "surfaceEntities" : qUnion([Q1]), "oppositeDirection" : true, "depth" : 25 * mm, "offsetDistance" : 25 * mm});
        }
    });
